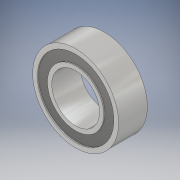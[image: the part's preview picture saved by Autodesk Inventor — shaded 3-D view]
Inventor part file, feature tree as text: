
AUTODESK INVENTOR PART (.ipt)
format: ipt  version: 2017 (Build 210142000, 142)  size: 140,800 bytes
history: native  units: in
note: dims shown in document units (in); Inventor stores cm internally (conversion verified against a paired STEP export)
features: extrude x3, sketch x3, projected_geometry x1
ambient origin geometry x8: Origin, YZ Plane, XZ Plane, XY Plane, X Axis, Y Axis, Z Axis, Center Point
bodies: Solid1 (feature_tree)
feature tree (7):
  extrude  "Extrusion1"  Depth=0.1969in
  extrude  "Extrusion2"  Depth=0.1181in
  extrude  "Extrusion3"  Depth=0.0039in TaperAngle=0.0deg
  sketch  "Sketch1"  dims[d0=0.3543in d1=0.1969in]
  sketch  "Sketch2"  dims[d2=0.1181in d3=0.0in d4=0.2323in]
  projected_geometry  "Projected Loop1"
  sketch  "Sketch3"  dims[d5=0.0197in d6=0.0039in d7=0.0in d8=0.0039in d9=0.0in]
